# Revit family: Zumtobel LITECOM touch panel
name_source: partatom
category: Lighting Devices
units: mm (PartAtom-declared; Revit-internal decimal feet)

## family parameters
Cut with Voids When Loaded = Yes
Host = Face
Maintain Annotation Orientation = No
OmniClass Number = 23.85.80.11.27
OmniClass Title = Lighting Controls
Part Type = Normal
Room Calculation Point = Yes
Round Connector Dimension = Use Diameter
Shared = No

## types (3) — shared parameters
Assembly Code = D5030800
Default Elevation = 1200 mm
Description = Touch Panel
Manufacturer = Zumtobel Lighting
Type Image = LITECOM-Touch panel.jpg
URL = https://www.zumtobel.com

## per-type parameters (varying)
| type | Model | Mounting Box Recessed | Mounting Box Surface Mounted | Offset | Visible Mounting Box Surface Mounted | Visible not Mounting Box | Void Depth | Void Height | Void Width |
| LITECOM Touchpanel 2 TCI | 24165702 | No | No | 12 mm  [stored 0.0393701 ft] | No | Yes | -50 mm  [stored -0.164042 ft] | 110 mm  [stored 0.360892 ft] | 160 mm  [stored 0.524934 ft] |
| LITECOM Touchpanel 2 TCI + MRW Touchpanel TCI | 24165702 + 28000376 | Yes | No | 1 mm  [stored 0.00328084 ft] | No | No | -80 mm  [stored -0.262467 ft] | 126 mm  [stored 0.413386 ft] | 190 mm  [stored 0.62336 ft] |
| LITECOM Touchpanel 2 TCI + MSW Touchpanel TCI | 24165702 + 24165674 | No | Yes | 49 mm  [stored 0.160761 ft] | Yes | No | 10 mm  [stored 0.0328084 ft] | 110 mm  [stored 0.360892 ft] | 160 mm  [stored 0.524934 ft] |

note: [stored X ft] marks values corroborated as IEEE doubles in the binary element streams (Revit-internal decimal feet)

## geometry (parser evidence)
native form markers: Sweep x2
no freeform markers — native parametric forms only
